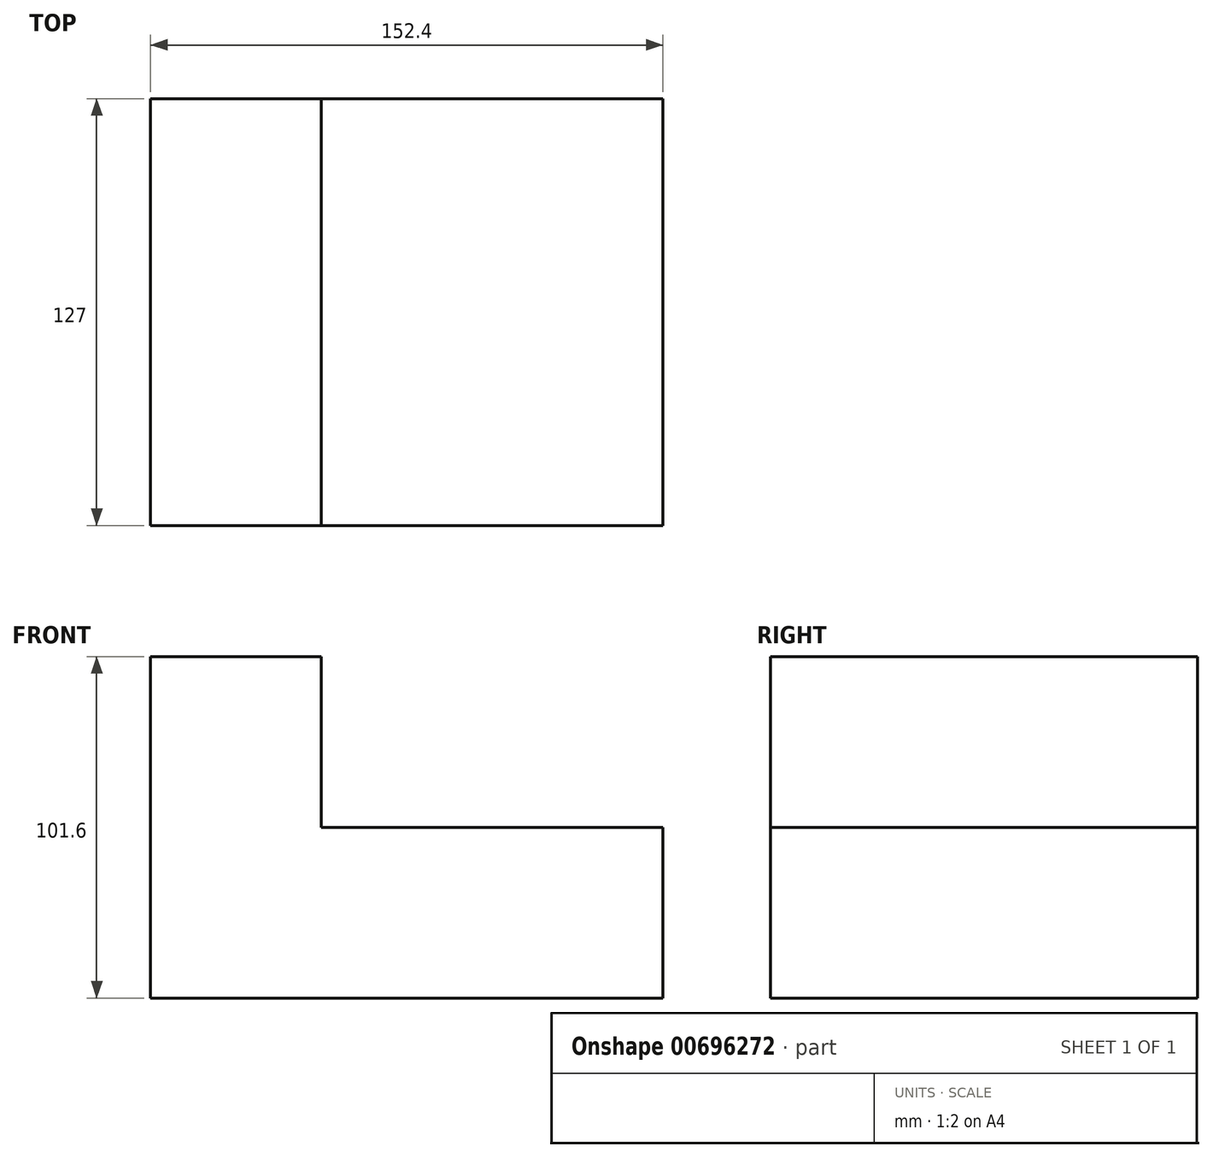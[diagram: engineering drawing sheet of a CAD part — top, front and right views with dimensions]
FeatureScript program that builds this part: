
annotation { "Feature Type Name" : "Feature", "Feature Type Description" : "" }
export const myFeature = defineFeature(function(context is Context, id is Id, definition is map)
    precondition{}
    {
        {
            var Q0;
            Q0=qCreatedBy(makeId("Front.planeOp"),FACE);
            var sketch = newSketch(context, id + "F0", { "sketchPlane" : qUnion([Q0])});
            skLineSegment(sketch, "E0", {"start": v(-75.58, -34.97) * mm, "end": v(76.82, -34.97) * mm});
            skLineSegment(sketch, "E1", {"start": v(-75.58, -34.97) * mm, "end": v(-75.58, 66.63) * mm});
            skLineSegment(sketch, "E2", {"start": v(-75.58, 66.63) * mm, "end": v(-24.78, 66.63) * mm});
            skLineSegment(sketch, "E3", {"start": v(-24.78, 66.63) * mm, "end": v(-24.78, 15.83) * mm});
            skLineSegment(sketch, "E4", {"start": v(-24.78, 15.83) * mm, "end": v(76.82, 15.83) * mm});
            skLineSegment(sketch, "E5", {"start": v(76.82, 15.83) * mm, "end": v(76.82, -34.97) * mm});
            skSolve(sketch);
        }
        {
            var Q0;
            Q0=makeQuery(id+"F0.imprint","IMPRINT",FACE,{"disambiguationData":[TD([[makeQuery(id+"F0.imprint","IMPRINT",EDGE,{"derivedFrom":sQuery(id+"F0.wireOp",EDGE,"E0")}),1.0]])]});
            extrude(context, id + "F1", {"entities" : qUnion([Q0]), "depth" : 127 * mm, "offsetDistance" : 25.4 * mm});
        }
    });
